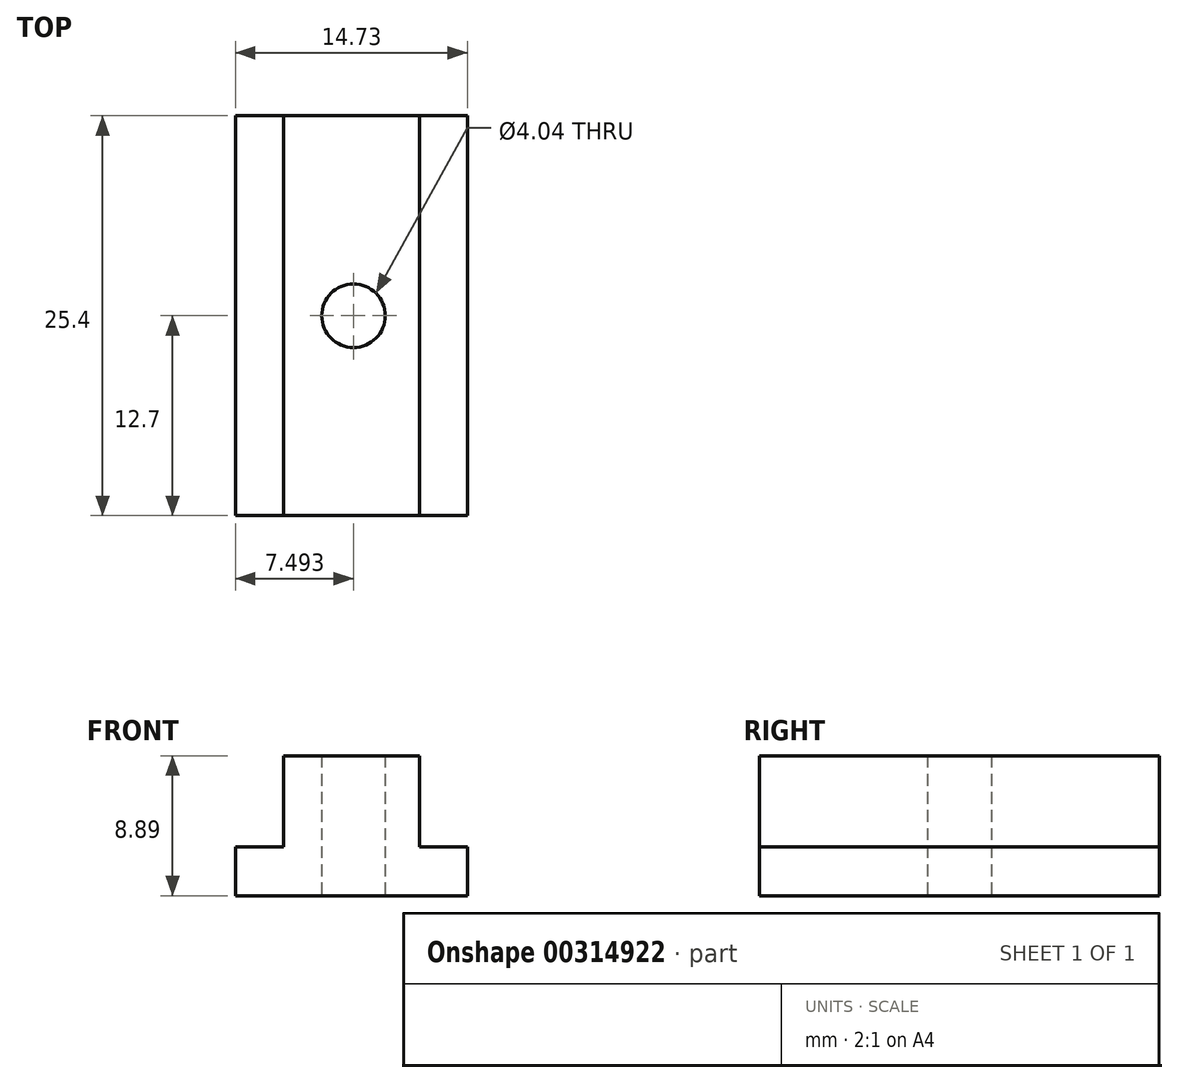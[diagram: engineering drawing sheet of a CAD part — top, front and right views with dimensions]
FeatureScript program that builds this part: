
annotation { "Feature Type Name" : "Feature", "Feature Type Description" : "" }
export const myFeature = defineFeature(function(context is Context, id is Id, definition is map)
    precondition{}
    {
        {
            var Q0;
            Q0=qCreatedBy(makeId("Front.planeOp"),FACE);
            var sketch = newSketch(context, id + "F0", { "sketchPlane" : qUnion([Q0])});
            skLineSegment(sketch, "E0", {"start": v(0, 0) * mm, "end": v(14.73, 0) * mm});
            skLineSegment(sketch, "E1", {"start": v(14.73, 0) * mm, "end": v(14.73, 3.1) * mm});
            skLineSegment(sketch, "E2", {"start": v(14.73, 3.1) * mm, "end": v(11.68, 3.1) * mm});
            skLineSegment(sketch, "E3", {"start": v(11.68, 3.1) * mm, "end": v(11.68, 8.9) * mm});
            skLineSegment(sketch, "E4", {"start": v(11.68, 8.9) * mm, "end": v(3.05, 8.9) * mm});
            skLineSegment(sketch, "E5", {"start": v(3.05, 8.89) * mm, "end": v(3.05, 3.1) * mm});
            skLineSegment(sketch, "E6", {"start": v(3.05, 3.1) * mm, "end": v(0, 3.1) * mm});
            skLineSegment(sketch, "E7", {"start": v(0, 3.1) * mm, "end": v(0, 0) * mm});
            skSolve(sketch);
        }
        {
            var Q0;
            Q0=makeQuery(id+"F0.imprint","IMPRINT",FACE,{"disambiguationData":[TD([[makeQuery(id+"F0.imprint","IMPRINT",EDGE,{"derivedFrom":sQuery(id+"F0.wireOp",EDGE,"E0")}),1.0]])]});
            extrude(context, id + "F1", {"entities" : qUnion([Q0]), "oppositeDirection" : true, "depth" : 25.4 * mm});
        }
        {
            var Q0;
            Q0=qCreatedBy(makeId("Top.planeOp"),FACE);
            var sketch = newSketch(context, id + "F2", { "sketchPlane" : qUnion([Q0])});
            skCircle(sketch, "E8", {"center": v(7.5, 12.7) * mm, "radius": 2.02 * mm});
            skSolve(sketch);
        }
        {
            var Q0;
            Q0 = qSketchRegion(id + "F2", true);
            extrude(context, id + "F3", {"entities" : qUnion([Q0]), "operationType" : NewBodyOperationType.REMOVE, "endBound" : BoundingType.THROUGH_ALL, "depth" : 25.4 * mm});
        }
    });
